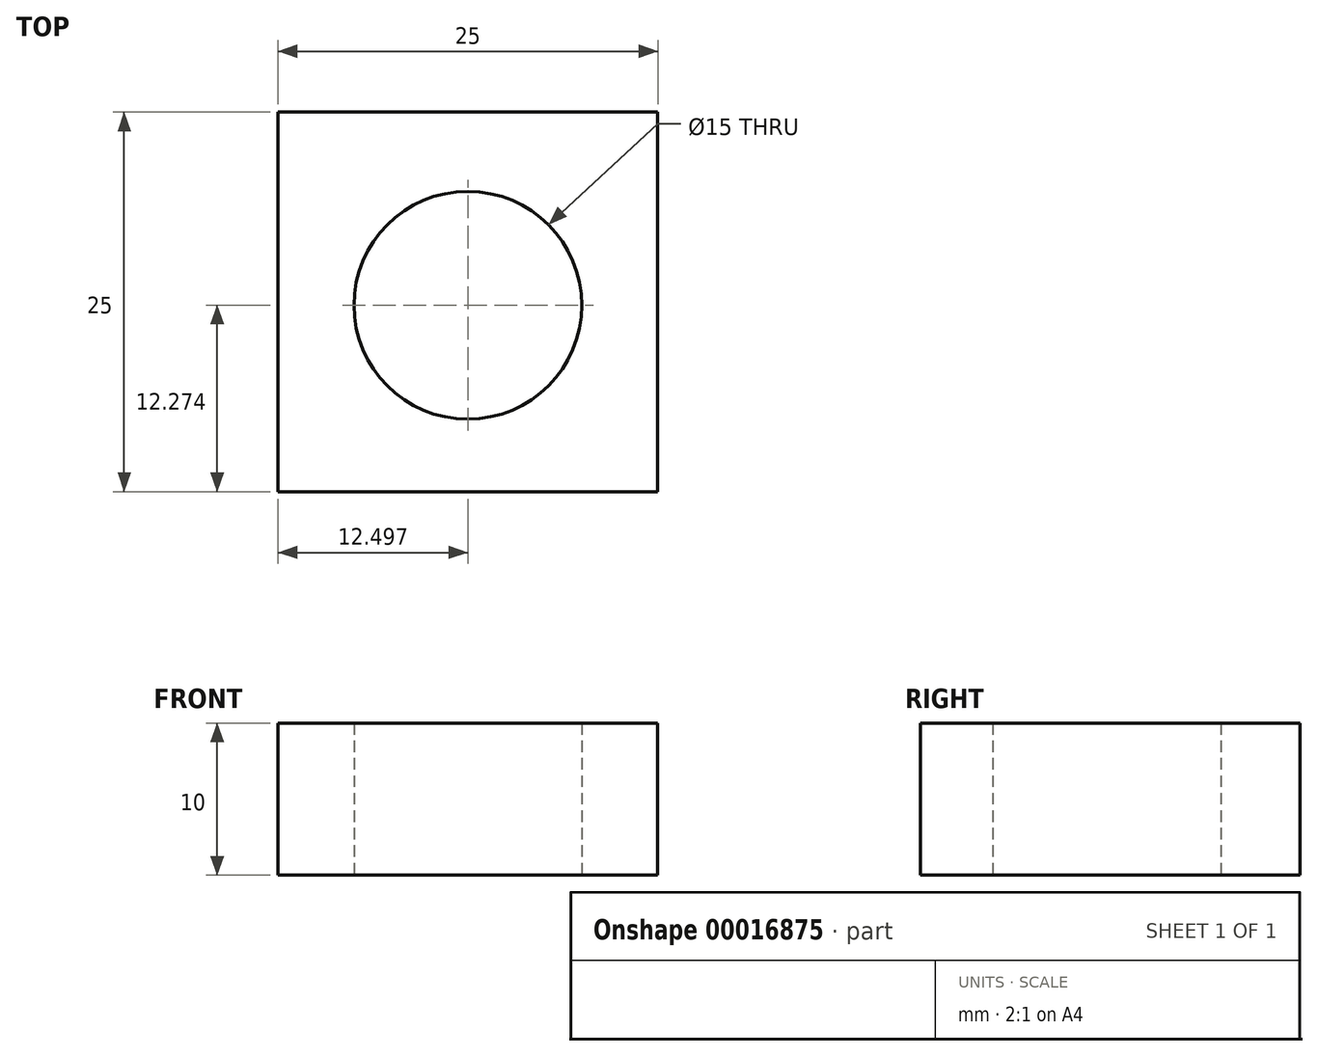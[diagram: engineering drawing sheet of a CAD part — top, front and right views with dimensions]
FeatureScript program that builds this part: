
annotation { "Feature Type Name" : "Feature", "Feature Type Description" : "" }
export const myFeature = defineFeature(function(context is Context, id is Id, definition is map)
    precondition{}
    {
        {
            var Q0;
            Q0=qCreatedBy(makeId("Top.planeOp"),FACE);
            var sketch = newSketch(context, id + "F0", { "sketchPlane" : qUnion([Q0])});
            skLineSegment(sketch, "E0.bottom", {"start": v(-7.25, 13.07) * mm, "end": v(17.75, 13.07) * mm});
            skLineSegment(sketch, "E0.top", {"start": v(-7.25, -11.93) * mm, "end": v(17.75, -11.93) * mm});
            skLineSegment(sketch, "E0.left", {"start": v(-7.25, 13.07) * mm, "end": v(-7.25, -11.93) * mm});
            skLineSegment(sketch, "E0.right", {"start": v(17.75, 13.07) * mm, "end": v(17.75, -11.93) * mm});
            skCircle(sketch, "E1", {"center": v(5.25, 0.34) * mm, "radius": 7.5 * mm});
            skSolve(sketch);
        }
        {
            var Q0;
            Q0=makeQuery(id+"F0.imprint","IMPRINT",FACE,{"disambiguationData":[TD([[makeQuery(id+"F0.imprint","IMPRINT",EDGE,{"derivedFrom":sQuery(id+"F0.wireOp",EDGE,"E0.bottom")}),-1.0]])]});
            extrude(context, id + "F1", {"entities" : qUnion([Q0]), "depth" : 10 * mm});
        }
    });
